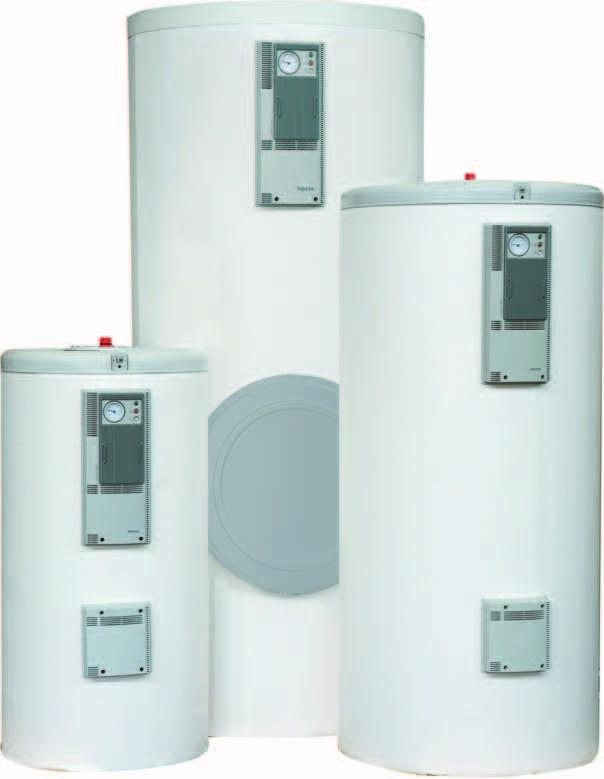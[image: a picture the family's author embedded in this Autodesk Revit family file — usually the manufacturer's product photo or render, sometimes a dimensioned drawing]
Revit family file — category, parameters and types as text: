
# Revit family: CV-300-HL_CC01791
name_source: partatom
category: Aparatos eléctricos
revit_build: Autodesk Revit 2016 (Build: 20150220_1215(x64)
units: mm (PartAtom-declared; Revit-internal decimal feet)

## family parameters
Compartido = No
Corte con vacíos al cargar = No
Cota de conector redondo = Diámetro de uso
Mantener orientación de anotación = No
Número OmniClass = 23.80.00.00
Punto de cálculo de habitación = No
Se basa en plano de trabajo = No
Siempre vertical = Sí
Tipo de pieza = Caja de conexiones
Título OmniClass = Electric Power and Lighting

## types (1)
- CV-200-HL
    Capacidad A.C.S. = 300 l
    Clase eficiencia energética = B
    Costo = 0 $
    Código de montaje = CC01791
    Descripción = DEPOSITOS DE ACERO VITRIFICADO
    Dimensiones = 620 x 1685 mm
    Fabricante = SALVADOR ESCODA
    Imagen de tipo = depositos_acero_vitrificado.jpg
    Modelo = CV-300-HL
    Peso vacío (aprox.) = 130 Kg
    Presión máx. circuito calentamiento = 2,5 (25) MPa (bar)
    Presión máx. depósito = 0,8 (8) MPa (bar)
    Pérdidas estáticas = 67 W
    Superfície intercambio circuito calentamiento = 3,1 m2
    Temperatura máx. circuito calentamiento = 200 ºC
    Temperatura máx. depósito = 90 ºC
    URL = www.salvadorescoda.com
    Volúmen = 292 l
